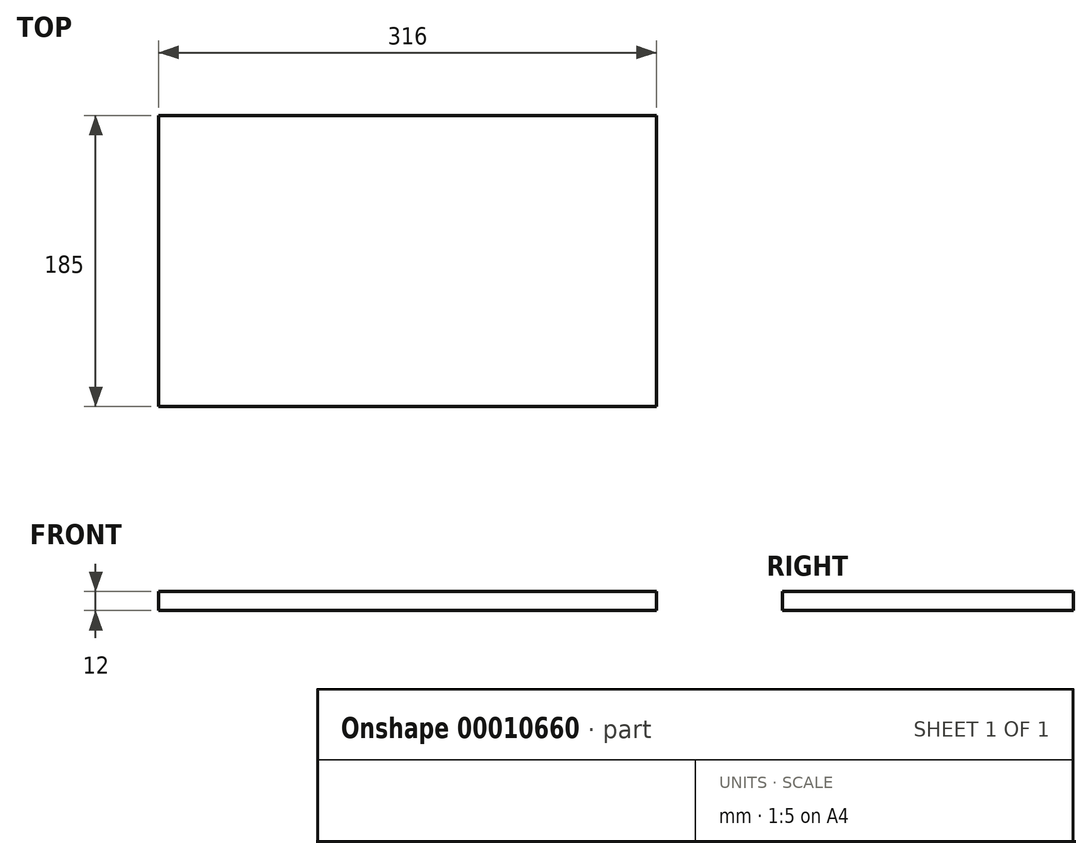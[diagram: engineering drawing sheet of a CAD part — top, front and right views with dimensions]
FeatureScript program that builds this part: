
annotation { "Feature Type Name" : "Feature", "Feature Type Description" : "" }
export const myFeature = defineFeature(function(context is Context, id is Id, definition is map)
    precondition{}
    {
        {
            var Q0;
            Q0=qCreatedBy(makeId("Top.planeOp"),FACE);
            var sketch = newSketch(context, id + "F0", { "sketchPlane" : qUnion([Q0])});
            skLineSegment(sketch, "E0.bottom", {"start": v(0, 0) * mm, "end": v(316, 0) * mm});
            skLineSegment(sketch, "E0.top", {"start": v(0, 185) * mm, "end": v(316, 185) * mm});
            skLineSegment(sketch, "E0.left", {"start": v(0, 0) * mm, "end": v(0, 185) * mm});
            skLineSegment(sketch, "E0.right", {"start": v(316, 0) * mm, "end": v(316, 185) * mm});
            skSolve(sketch);
        }
        {
            var Q0;
            Q0=makeQuery(id+"F0.imprint","IMPRINT",FACE,{"disambiguationData":[TD([[makeQuery(id+"F0.imprint","IMPRINT",EDGE,{"derivedFrom":sQuery(id+"F0.wireOp",EDGE,"E0.bottom")}),1.0]])]});
            extrude(context, id + "F1", {"entities" : qUnion([Q0]), "depth" : 12 * mm});
        }
    });
